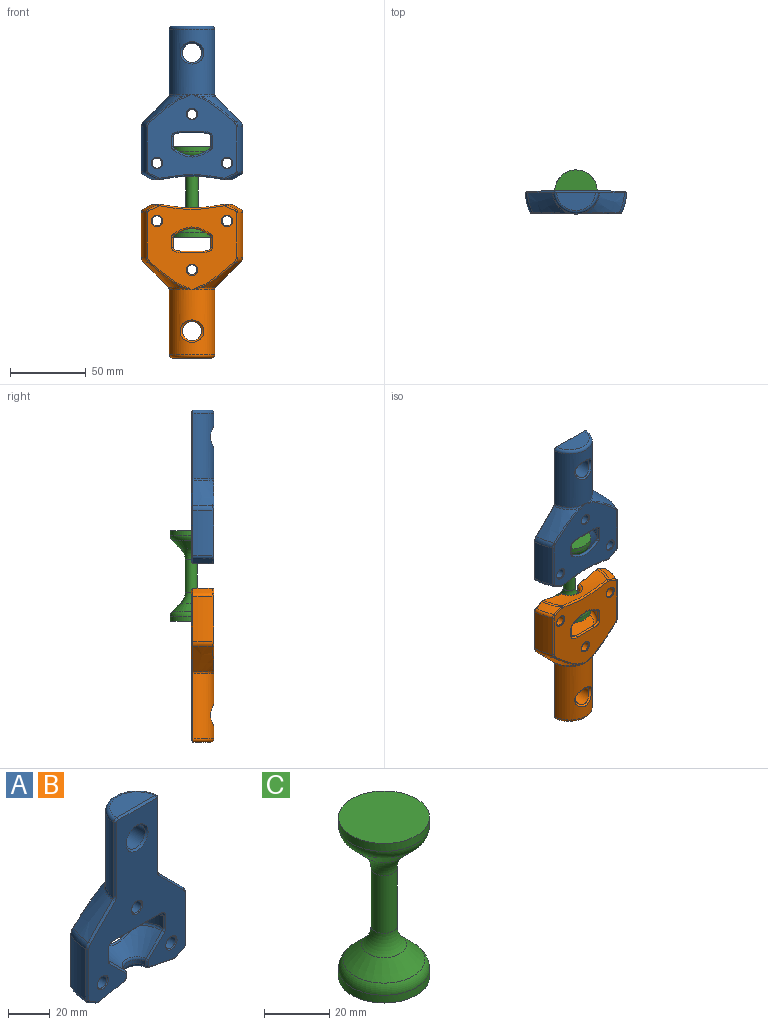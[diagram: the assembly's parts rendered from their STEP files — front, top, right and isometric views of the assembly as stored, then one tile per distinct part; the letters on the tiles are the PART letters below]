
ASSEMBLY  parts=3 mates=3
PART A: 102 faces, bbox 72.9x30.6x103.9 mm
  f0: cone r=26mm half-angle=61.9deg, axis (0,0,1), area 85mm2, adj f17,f21,f55,f86
  f1: cone r=26mm half-angle=61.9deg, axis (0,0,1), area 85mm2, adj f18,f22,f46,f90
  f2: cylinder r=33.5mm len=29.64mm, axis (0,0,-1), area 411.7mm2, adj f16,f18,f42,f92
  f3: cylinder r=33.5mm len=29.64mm, axis (0,0,-1), area 411.7mm2, adj f15,f17,f51,f84
  f4: plane 31.94x13.01mm, normal (0,0,-1), area 349.4mm2, adj f19,f20,f66,f74
  f5: cylinder r=18.5mm len=12.33mm, axis (0,0,-1), area 92.5mm2, adj f11,f20,f62,f75
  f6: cylinder r=18.5mm len=12.33mm, axis (0,0,-1), area 92.5mm2, adj f12,f19,f70,f78
  f7: cone r=6.5mm half-angle=45deg, axis (0,0,1), area 568.5mm2, adj f11,f12,f27,f58,f67,f79
  f8: cone r=6.5mm half-angle=78.4deg, axis (0,0,-1), area 515.6mm2, adj f21,f22,f34,f50,f59,f88
  f9: cone r=15mm half-angle=45deg, axis (0,0,-1), area 417mm2, adj f14,f15,f47,f82
  f10: cone r=15mm half-angle=45deg, axis (0,0,-1), area 417mm2, adj f13,f16,f38,f95
  f11: torus R=16.5mm, axis (0,0,-1), area 22.2mm2, adj f5,f7,f60,f77
  f12: torus R=16.5mm, axis (0,0,-1), area 22.2mm2, adj f6,f7,f69,f80
  f13: torus R=17mm, axis (0,0,-1), area 31.7mm2, adj f10,f24,f36,f93
  f14: torus R=17mm, axis (0,0,-1), area 31.7mm2, adj f9,f24,f45,f81
  f15: torus R=28.5mm, axis (0,0,1), area 54.8mm2, adj f3,f9,f49,f83
  f16: torus R=28.5mm, axis (0,0,1), area 54.8mm2, adj f2,f10,f40,f94
  f17: torus R=31mm, axis (0,0,1), area 37.5mm2, adj f0,f3,f53,f85
  f18: torus R=31mm, axis (0,0,1), area 37.5mm2, adj f1,f2,f44,f91
  f19: torus R=16mm, axis (0,0,1), area 60.3mm2, adj f4,f6,f68,f76
  f20: torus R=16mm, axis (0,0,1), area 60.3mm2, adj f4,f5,f64,f73
  f21: torus R=25.62mm, axis (0,0,1), area 24mm2, adj f0,f8,f57,f87
  f22: torus R=25.62mm, axis (0,0,1), area 24mm2, adj f1,f8,f48,f89
  f23: cylinder r=6.5mm len=12.88mm, axis (0,0,-1), area 39.8mm2, adj f27,f34,f54,f63
  f24: cylinder r=15mm len=43.27mm, axis (0,0,-1), area 1754.8mm2, adj f13,f14,f28,f35,f43,f72
  f25: plane 25.92x12mm, normal (0,0,1), area 239.5mm2, adj f28,f39
  f26: plane 99.75x65mm, normal (0,-1,0), area 3176.3mm2, adj f35,f36,f37,f38,f39,f40,f41,f42
  f27: torus R=8.5mm, axis (0,0,1), area 30.3mm2, adj f7,f23,f56,f65
  f28: torus R=13mm, axis (0,0,1), area 134.2mm2, adj f24,f25,f37,f41
  f29: cylinder r=6.4mm len=13mm, axis (0,-1,0), area 522.8mm2, adj f71,f72
  f30: plane 59.08x55.83mm, normal (0,1,0), area 2135.9mm2, adj f73,f74,f75,f76,f77,f78,f79,f80
  f31: cylinder r=3.3mm len=14mm, axis (0,-1,0), area 290.3mm2, adj f98,f99
  f32: cylinder r=3.3mm len=14mm, axis (0,-1,0), area 290.3mm2, adj f96,f101
  f33: cylinder r=3.3mm len=14mm, axis (0,-1,0), area 290.3mm2, adj f97,f100
  f34: torus R=9mm, axis (0,0,1), area 71.4mm2, adj f8,f23,f52,f61
  f35: plane 43.27x1.07mm, normal (0.73,-0.68,0), area 63.3mm2, adj f24,f26,f36,f37
  f36: bspline ~2.12x1.59mm, area 2.9mm2, adj f13,f26,f35,f38
  f37: bspline ~2.03x2.03mm, area 3.4mm2, adj f26,f28,f35,f39
  f38: bspline ~17.18x17.16mm, area 33.5mm2, adj f10,f26,f36,f40
  f39: plane 25.92x1mm, normal (0,-0.71,0.71), area 36.7mm2, adj f25,f26,f37,f41
  f40: bspline ~3.54x2.18mm, area 5.1mm2, adj f16,f26,f38,f42
  f41: bspline ~2.03x2.03mm, area 3.4mm2, adj f26,f28,f39,f43
  f42: plane 29.64x1.03mm, normal (0.72,-0.7,0), area 42.6mm2, adj f2,f26,f40,f44
  f43: plane 43.27x1.07mm, normal (-0.73,-0.68,0), area 63.3mm2, adj f24,f26,f41,f45
  f44: bspline ~2.21x1.8mm, area 3.1mm2, adj f18,f26,f42,f46
  f45: bspline ~2.12x1.59mm, area 2.9mm2, adj f14,f26,f43,f47
  f46: bspline ~5.85x3.75mm, area 8.7mm2, adj f1,f26,f44,f48
  f47: bspline ~17.18x17.16mm, area 33.5mm2, adj f9,f26,f45,f49
  f48: bspline ~1.68x1.24mm, area 2mm2, adj f22,f26,f46,f50
  f49: bspline ~3.54x2.18mm, area 5.1mm2, adj f15,f26,f47,f51
  f50: bspline ~16.86x4.39mm, area 23.9mm2, adj f8,f26,f48,f52
  f51: plane 29.64x1.03mm, normal (-0.72,-0.7,0), area 42.6mm2, adj f3,f26,f49,f53
  f52: bspline ~2.45x2.22mm, area 3.7mm2, adj f26,f34,f50,f54
  f53: bspline ~2.21x1.8mm, area 3.1mm2, adj f17,f26,f51,f55
  f54: plane 2.13x0.99mm, normal (-0.66,-0.75,0), area 2.8mm2, adj f23,f26,f52,f56
  f55: bspline ~5.85x3.75mm, area 8.7mm2, adj f0,f26,f53,f57
  f56: bspline ~1.41x1.29mm, area 1.6mm2, adj f26,f27,f54,f58
  f57: bspline ~1.68x1.24mm, area 2mm2, adj f21,f26,f55,f59
  f58: bspline ~11.57x11.54mm, area 21.1mm2, adj f7,f26,f56,f60
  f59: bspline ~16.86x4.39mm, area 23.9mm2, adj f8,f26,f57,f61
  f60: bspline ~2.12x1.59mm, area 2.7mm2, adj f11,f26,f58,f62
  f61: bspline ~2.45x2.22mm, area 3.7mm2, adj f26,f34,f59,f63
  f62: plane 6.67x1mm, normal (-0.69,-0.73,0), area 9.2mm2, adj f5,f26,f60,f64
  f63: plane 2.13x0.99mm, normal (0.66,-0.75,0), area 2.8mm2, adj f23,f26,f61,f65
  f64: bspline ~3.51x3.5mm, area 6.6mm2, adj f20,f26,f62,f66
  f65: bspline ~1.41x1.29mm, area 1.6mm2, adj f26,f27,f63,f67
  f66: plane 31.94x1mm, normal (0,-0.71,-0.71), area 45mm2, adj f4,f26,f64,f68
  f67: bspline ~11.57x11.54mm, area 21.1mm2, adj f7,f26,f65,f69
  f68: bspline ~3.55x3.55mm, area 6.6mm2, adj f19,f26,f66,f70
  f69: bspline ~2.12x1.59mm, area 2.7mm2, adj f12,f26,f67,f70
  f70: plane 6.67x1mm, normal (0.69,-0.73,0), area 9.2mm2, adj f6,f26,f68,f69
  f71: cone r=6.4mm half-angle=45deg, axis (0,-1,0), area 61.3mm2, adj f26,f29
  f72: bspline ~15.87x14.81mm, area 71.6mm2, adj f24,f29
  f73: bspline ~6.42x3.65mm, area 12.8mm2, adj f20,f30,f74,f75
  f74: cylinder r=1mm len=15.49mm, axis (-1,0,0), area 24.3mm2, adj f4,f30,f73,f76
  f75: cylinder r=1mm len=6.67mm, axis (0,0,-1), area 15.8mm2, adj f5,f30,f73,f77
  f76: bspline ~6.42x4.1mm, area 12.8mm2, adj f19,f30,f74,f78
  f77: bspline ~3.1x2.74mm, area 4.3mm2, adj f11,f30,f75,f79
  f78: cylinder r=1mm len=6.67mm, axis (0,0,-1), area 15.8mm2, adj f6,f30,f76,f80
  f79: bspline ~30.56x8.09mm, area 58.3mm2, adj f7,f30,f77,f80
  f80: bspline ~3.1x2.74mm, area 4.3mm2, adj f12,f30,f78,f79
  f81: bspline ~5.28x2.12mm, area 1.5mm2, adj f14,f30,f82
  f82: bspline ~31.68x22.09mm, area 31mm2, adj f9,f30,f81,f83
  f83: bspline ~5.31x3.04mm, area 4.3mm2, adj f15,f30,f82,f84
  f84: cylinder r=1mm len=29.64mm, axis (0,0,-1), area 33.4mm2, adj f3,f30,f83,f85
  f85: bspline ~2.56x2.17mm, area 2.8mm2, adj f17,f30,f84,f86
  f86: bspline ~17.42x8.79mm, area 9.1mm2, adj f0,f30,f85,f87
  f87: bspline ~2.74x1.3mm, area 2.4mm2, adj f21,f30,f86,f88
  f88: bspline ~52.69x4.9mm, area 73.2mm2, adj f8,f30,f87,f89
  f89: bspline ~2.74x1.3mm, area 2.4mm2, adj f22,f30,f88,f90
  f90: bspline ~15.83x8.11mm, area 9.1mm2, adj f1,f30,f89,f91
  f91: bspline ~2.95x2.17mm, area 2.8mm2, adj f18,f30,f90,f92
  f92: cylinder r=1mm len=29.64mm, axis (0,0,-1), area 33.4mm2, adj f2,f30,f91,f94
  f93: bspline ~6.6x2.53mm, area 1.5mm2, adj f13,f30,f95
  f94: bspline ~5.31x3.04mm, area 4.3mm2, adj f16,f30,f92,f95
  f95: bspline ~28.37x21.34mm, area 31mm2, adj f10,f30,f93,f94
  f96: cone r=3.3mm half-angle=45deg, axis (0,-1,0), area 15.8mm2, adj f26,f32
  f97: cone r=3.8mm half-angle=45deg, axis (0,-1,0), area 15.8mm2, adj f26,f33
  f98: cone r=3.3mm half-angle=45deg, axis (0,-1,0), area 15.8mm2, adj f26,f31
  f99: cone r=3.8mm half-angle=45deg, axis (0,1,0), area 15.8mm2, adj f30,f31
  f100: cone r=3.3mm half-angle=45deg, axis (0,1,0), area 15.8mm2, adj f30,f33
  f101: cone r=3.8mm half-angle=45deg, axis (0,1,0), area 15.8mm2, adj f30,f32
PART B: same geometry as A
PART C: 11 faces, bbox 30.3x30.3x60.6 mm
  f0: cylinder r=14mm len=28mm, axis (0,0,1), area 257.6mm2, adj f1,f10
  f1: plane 28x28mm, normal (0,0,1), area 615.8mm2, adj f0
  f2: plane 28x28mm, normal (0,0,-1), area 615.8mm2, adj f3
  f3: cylinder r=14mm len=28mm, axis (0,0,1), area 257.6mm2, adj f2,f9
  f4: cone r=14mm half-angle=45deg, axis (0,0,-1), area 484.8mm2, adj f7,f9
  f5: cylinder r=4mm len=21.72mm, axis (0,0,1), area 545.8mm2, adj f7,f8
  f6: cone r=4mm half-angle=45deg, axis (0,0,1), area 484.8mm2, adj f8,f10
  f7: torus R=14mm, axis (0,0,1), area 246.6mm2, adj f4,f5
  f8: torus R=14mm, axis (0,0,1), area 246.6mm2, adj f5,f6
  f9: torus R=9mm, axis (0,0,-1), area 333.1mm2, adj f3,f4
  f10: torus R=9mm, axis (0,0,-1), area 333.1mm2, adj f0,f6
PLACE A rot(axis=(0,0,-1),180deg) t=(178.33,162.81,227.64)mm
PLACE B rot(axis=(1,0,0),180deg) t=(178.33,162.81,193.53)mm
PLACE C rot(axis=(0.2,-0.98,0),180deg) t=(178.33,162.81,210.55)mm
MATE planar A.f26 <-> B.f26  axis (0,1,0) through (178.33,162.81,264.9)mm
MATE cylindrical B.f0 <-> A.f0  axis (0,0,1) through (178.33,162.81,124.35)mm
MATE cylindrical C.f0 <-> B.f0  axis (0,0,-1) through (178.33,162.81,210.55)mm
